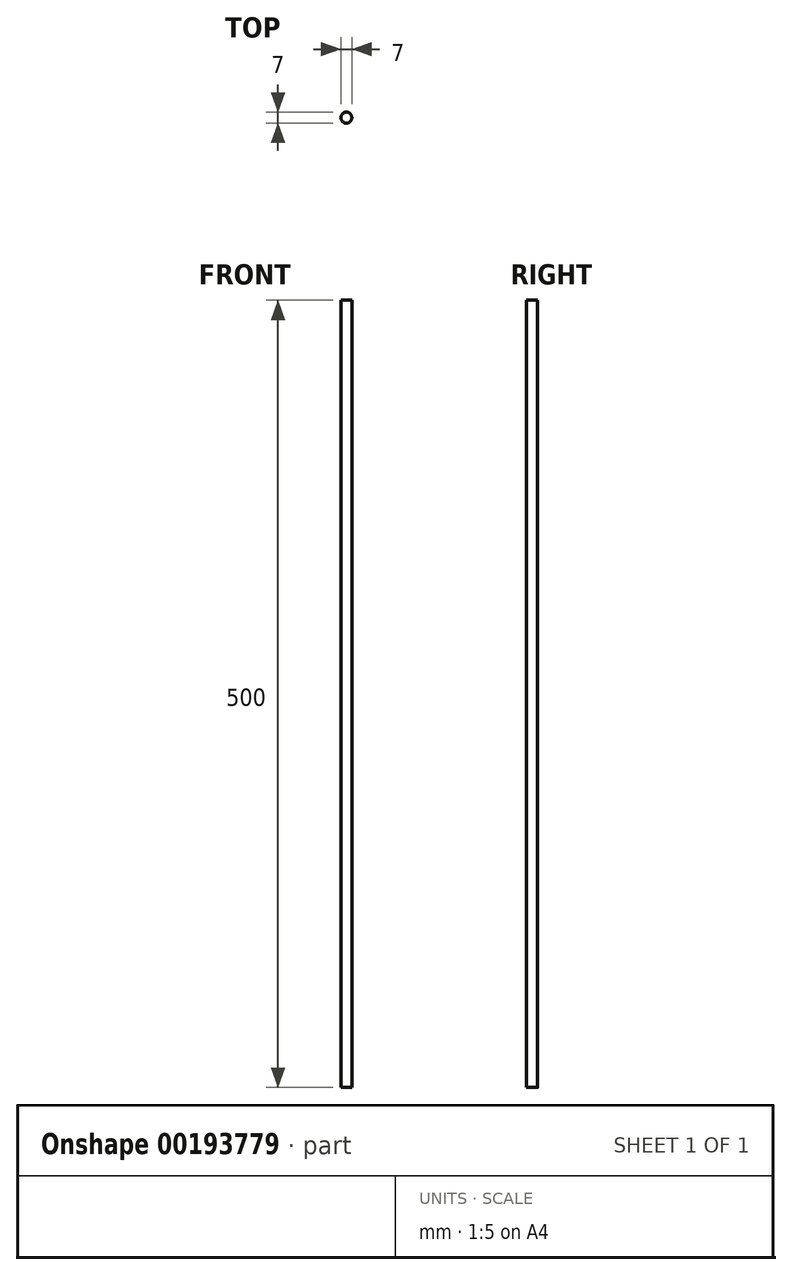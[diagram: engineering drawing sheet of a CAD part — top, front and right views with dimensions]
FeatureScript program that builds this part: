
annotation { "Feature Type Name" : "Feature", "Feature Type Description" : "" }
export const myFeature = defineFeature(function(context is Context, id is Id, definition is map)
    precondition{}
    {
        {
            var Q0;
            Q0=qCreatedBy(makeId("Top.planeOp"),FACE);
            var sketch = newSketch(context, id + "F0", { "sketchPlane" : qUnion([Q0])});
            skCircle(sketch, "E0", {"center": v(0, 0) * mm, "radius": 3.5 * mm});
            skSolve(sketch);
        }
        {
            var Q0;
            Q0 = qSketchRegion(id + "F0", true);
            extrude(context, id + "F1", {"entities" : qUnion([Q0]), "depth" : 500 * mm});
        }
    });
